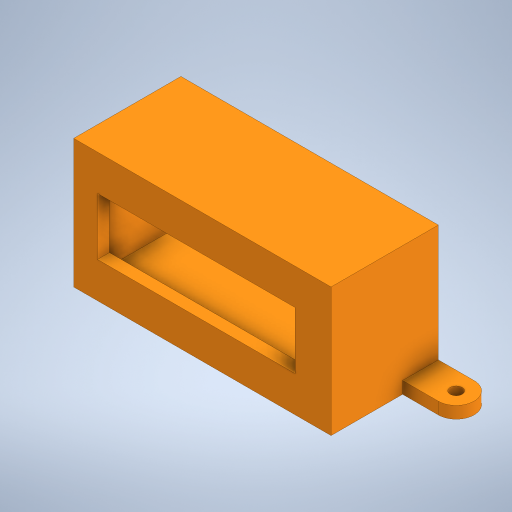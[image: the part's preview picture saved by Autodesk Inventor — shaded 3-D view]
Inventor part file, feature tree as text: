
AUTODESK INVENTOR PART (.ipt)
format: ipt  version: 2023 (Build 270158000, 158)  size: 261,120 bytes
history: native  units: mm
features: extrude x3, sketch x3
ambient origin geometry x8: Origin, YZ Plane, XZ Plane, XY Plane, X Axis, Y Axis, Z Axis, Center Point
bodies: Solid1 (feature_tree)
feature tree (6):
  extrude  "Extrusion1"  Depth=44.0mm
  extrude  "Extrusion2"  Depth=5.0mm
  extrude  "Extrusion3"  Depth=5.0mm
  sketch  "Sketch1"  dims[d0=98.0mm d1=44.0mm]
  sketch  "Sketch2"  dims[d2=5.0mm d3=5.0mm]
  sketch  "Sketch3"  dims[d4=5.0mm d5=5.0mm d6=40.0mm d7=0.0mm d8=5.0mm d9=0.0mm d10=10.0mm d11=15.0mm d12=15.0mm d13=15.0mm d14=15.0mm d15=15.0mm d16=5.0mm d17=5.0mm d18=0.0mm]
